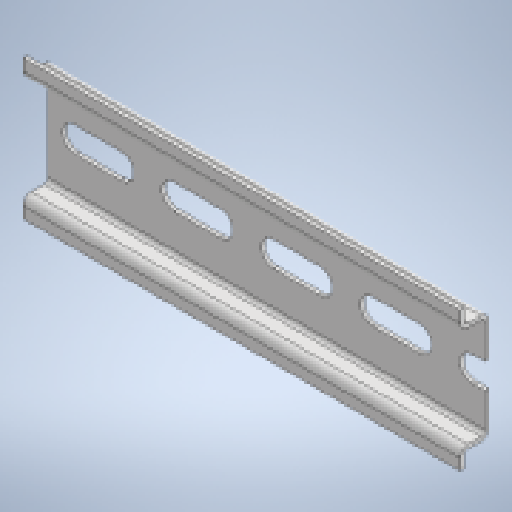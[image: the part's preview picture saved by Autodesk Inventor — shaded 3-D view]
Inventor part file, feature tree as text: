
AUTODESK INVENTOR PART (.ipt)
format: ipt  version: 2023 (Build 270158030, 158C)  size: 271,360 bytes
history: native  units: mm
features: other x4, extrude x3, sketch x3, reference x1
ambient origin geometry x8: Origin, YZ Plane, XZ Plane, XY Plane, X Axis, Y Axis, Z Axis, Center Point
bodies: Body1 (feature_tree)
feature tree (11):
  other  "DIN"
  extrude  "Extrusion1"  Depth=1.0mm
  extrude  "Extrusion2"  Depth=7.3mm
  extrude  "Extrusion3"  Depth=1.0mm
  sketch  "Sketch1"  dims[d0=1.0mm d1=1.0mm]
  reference  "Reference1"
  sketch  "Sketch2"  dims[d5=35.0mm d8=7.3mm]
  sketch  "Sketch3"  dims[d9=1.0mm d10=1.0mm d11=2.0mm d12=2.0mm d13=12.7mm d15=12.7mm d16=4.8mm d17=4.8mm d20=1.0mm d21=1.0mm d22=2.0mm d23=300.0mm d24=0.0mm d26=18.0mm d31=80.0mm d33=25.0mm d34=10.0mm d36=10.0mm d39=25.0mm d40=0.0mm d46=3.6mm d47=17.5mm d48=17.5mm d49=50.0mm d51=25.0mm d52=10.0mm d54=10.0mm d56=110.0mm d57=2.0mm d58=5.0mm d59=5.0mm d60=0.0mm d61=0.0mm]
  other  "<userpath>\Documents\0004-inventor\Inventor_Projects\electronics-enclosure\enclosure.iam"
  other  "enclosure.iam"
  other  "assembly-board:1"
